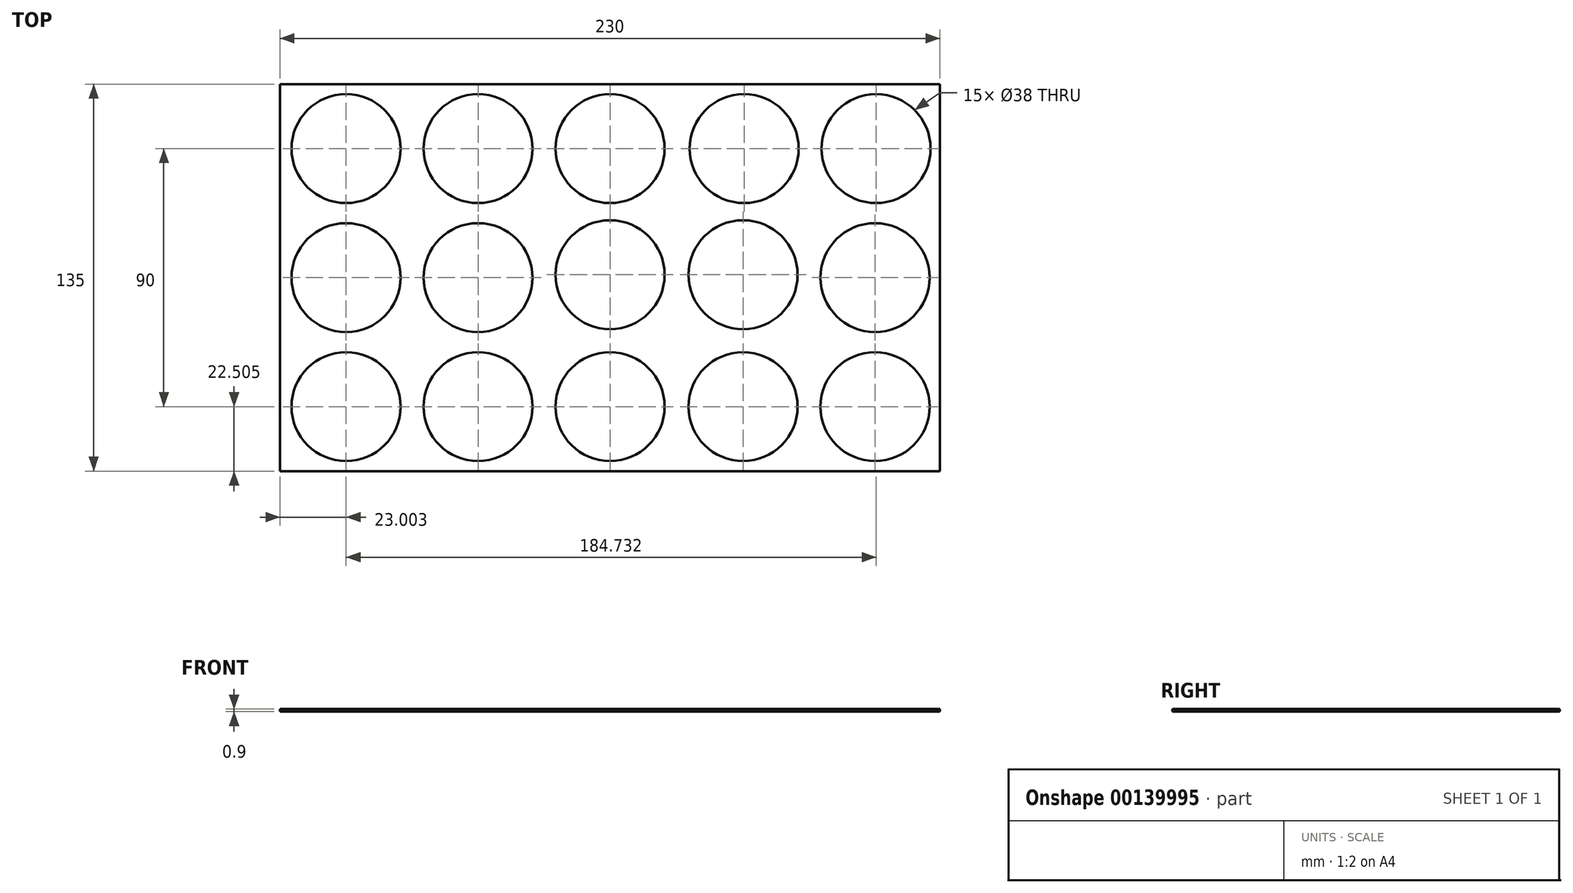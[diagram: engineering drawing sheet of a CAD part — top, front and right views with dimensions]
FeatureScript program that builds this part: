
annotation { "Feature Type Name" : "Feature", "Feature Type Description" : "" }
export const myFeature = defineFeature(function(context is Context, id is Id, definition is map)
    precondition{}
    {
        {
            var Q0;
            Q0=qCreatedBy(makeId("Top.planeOp"),FACE);
            var sketch = newSketch(context, id + "F0", { "sketchPlane" : qUnion([Q0])});
            skLineSegment(sketch, "E0.bottom", {"start": v(-102.59, 50.68) * mm, "end": v(127.41, 50.68) * mm});
            skLineSegment(sketch, "E0.top", {"start": v(-102.59, -84.32) * mm, "end": v(127.41, -84.32) * mm});
            skLineSegment(sketch, "E0.left", {"start": v(-102.59, 50.68) * mm, "end": v(-102.59, -84.32) * mm});
            skLineSegment(sketch, "E0.right", {"start": v(127.41, 50.68) * mm, "end": v(127.41, -84.32) * mm});
            skLineSegment(sketch, "E1", {"start": v(-102.59, -84.32) * mm, "end": v(-102.59, -39.32) * mm});
            skLineSegment(sketch, "E2", {"start": v(-102.59, -39.32) * mm, "end": v(-102.59, 5.68) * mm});
            skLineSegment(sketch, "E3", {"start": v(-102.59, 5.68) * mm, "end": v(-102.59, 50.68) * mm});
            skLineSegment(sketch, "E4", {"start": v(-102.59, -84.32) * mm, "end": v(-56.59, -84.32) * mm});
            skLineSegment(sketch, "E5", {"start": v(-56.59, -84.32) * mm, "end": v(-10.59, -84.32) * mm});
            skLineSegment(sketch, "E6", {"start": v(-10.59, -84.32) * mm, "end": v(35.41, -84.32) * mm});
            skLineSegment(sketch, "E7", {"start": v(35.41, -84.32) * mm, "end": v(81.41, -84.32) * mm});
            skLineSegment(sketch, "E8", {"start": v(81.41, -84.32) * mm, "end": v(127.41, -84.32) * mm});
            skCircle(sketch, "E9", {"center": v(-79.59, 28.18) * mm, "radius": 19 * mm});
            skCircle(sketch, "E10", {"center": v(-33.59, 28.18) * mm, "radius": 19 * mm});
            skCircle(sketch, "E11", {"center": v(12.41, 28.18) * mm, "radius": 19 * mm});
            skCircle(sketch, "E12", {"center": v(59.15, 28.18) * mm, "radius": 19 * mm});
            skCircle(sketch, "E13", {"center": v(105.15, 28.18) * mm, "radius": 19 * mm});
            skCircle(sketch, "E14", {"center": v(104.78, -16.82) * mm, "radius": 19 * mm});
            skCircle(sketch, "E15", {"center": v(104.78, -61.82) * mm, "radius": 19 * mm});
            skCircle(sketch, "E16", {"center": v(58.78, -61.82) * mm, "radius": 19 * mm});
            skCircle(sketch, "E17", {"center": v(58.78, -15.8) * mm, "radius": 19 * mm});
            skCircle(sketch, "E18", {"center": v(12.41, -15.8) * mm, "radius": 19 * mm});
            skCircle(sketch, "E19", {"center": v(12.41, -61.82) * mm, "radius": 19 * mm});
            skCircle(sketch, "E20", {"center": v(-33.59, -61.82) * mm, "radius": 19 * mm});
            skCircle(sketch, "E21", {"center": v(-33.59, -16.82) * mm, "radius": 19 * mm});
            skCircle(sketch, "E22", {"center": v(-79.59, -16.82) * mm, "radius": 19 * mm});
            skCircle(sketch, "E23", {"center": v(-79.59, -61.82) * mm, "radius": 19 * mm});
            skPoint(sketch, "E24", {"position": v(-56.59, -39.32) * mm});
            skPoint(sketch, "E25", {"position": v(-10.59, -39.32) * mm});
            skPoint(sketch, "E26", {"position": v(35.41, -39.32) * mm});
            skPoint(sketch, "E27", {"position": v(-14.59, -17.06) * mm});
            skPoint(sketch, "E28", {"position": v(-56.59, 5.68) * mm});
            skPoint(sketch, "E29", {"position": v(35.41, 5.68) * mm});
            skPoint(sketch, "E30", {"position": v(81.41, 5.68) * mm});
            skPoint(sketch, "E31", {"position": v(81.41, -39.32) * mm});
            skCircle(sketch, "E32", {"center": v(-56.59, -39.32) * mm, "radius": 2.5 * mm});
            skCircle(sketch, "E33", {"center": v(-10.59, -39.32) * mm, "radius": 2.5 * mm});
            skCircle(sketch, "E34", {"center": v(35.41, -39.32) * mm, "radius": 2.5 * mm});
            skCircle(sketch, "E35", {"center": v(81.41, -39.32) * mm, "radius": 2.5 * mm});
            skCircle(sketch, "E36", {"center": v(81.41, 5.68) * mm, "radius": 2.5 * mm});
            skCircle(sketch, "E37", {"center": v(35.41, 5.68) * mm, "radius": 2.5 * mm});
            skCircle(sketch, "E38", {"center": v(-56.59, 5.68) * mm, "radius": 2.5 * mm});
            skPoint(sketch, "E39", {"position": v(-10.59, 5.68) * mm});
            skCircle(sketch, "E40", {"center": v(-10.59, 5.68) * mm, "radius": 2.5 * mm});
            skSolve(sketch);
        }
        {
            var Q0;
            Q0=makeQuery(id+"F0.imprint","IMPRINT",FACE,{"disambiguationData":[TD([[makeQuery(id+"F0.imprint","IMPRINT",EDGE,{"derivedFrom":sQuery(id+"F0.wireOp",EDGE,"E0.bottom")}),-1.0]])]});
            extrude(context, id + "F1", {"entities" : qUnion([Q0]), "depth" : 0.9 * mm});
        }
        {
            var Q0;
            Q0=sQuery(id+"F0.wireOp",EDGE,"E38");
            var Q1;
            Q1=sQuery(id+"F0.wireOp",EDGE,"E32");
            var Q2;
            Q2=sQuery(id+"F0.wireOp",EDGE,"E33");
            var Q3;
            Q3=sQuery(id+"F0.wireOp",EDGE,"E40");
            var Q4;
            Q4=sQuery(id+"F0.wireOp",EDGE,"E37");
            var Q5;
            Q5=sQuery(id+"F0.wireOp",EDGE,"E34");
            var Q6;
            Q6=sQuery(id+"F0.wireOp",EDGE,"E35");
            var Q7;
            Q7=sQuery(id+"F0.wireOp",EDGE,"E36");
            extrude(context, id + "F2", {"bodyType" : ToolBodyType.SURFACE, "surfaceEntities" : qUnion([Q0, Q1, Q2, Q3, Q4, Q5, Q6, Q7]), "oppositeDirection" : true, "depth" : 27 * mm});
        }
        {
            var Q0;
            Q0=makeQuery(id+"F0.imprint","IMPRINT",FACE,{"disambiguationData":[TD([[makeQuery(id+"F0.imprint","IMPRINT",EDGE,{"derivedFrom":sQuery(id+"F0.wireOp",EDGE,"E34")}),1.0]])]});
            var Q1;
            Q1=makeQuery(id+"F0.imprint","IMPRINT",FACE,{"disambiguationData":[TD([[makeQuery(id+"F0.imprint","IMPRINT",EDGE,{"derivedFrom":sQuery(id+"F0.wireOp",EDGE,"E35")}),1.0]])]});
            var Q2;
            Q2=makeQuery(id+"F0.imprint","IMPRINT",FACE,{"disambiguationData":[TD([[makeQuery(id+"F0.imprint","IMPRINT",EDGE,{"derivedFrom":sQuery(id+"F0.wireOp",EDGE,"E36")}),1.0]])]});
            var Q3;
            Q3=makeQuery(id+"F0.imprint","IMPRINT",FACE,{"disambiguationData":[TD([[makeQuery(id+"F0.imprint","IMPRINT",EDGE,{"derivedFrom":sQuery(id+"F0.wireOp",EDGE,"E37")}),1.0]])]});
            var Q4;
            Q4=makeQuery(id+"F0.imprint","IMPRINT",FACE,{"disambiguationData":[TD([[makeQuery(id+"F0.imprint","IMPRINT",EDGE,{"derivedFrom":sQuery(id+"F0.wireOp",EDGE,"E40")}),1.0]])]});
            var Q5;
            Q5=makeQuery(id+"F0.imprint","IMPRINT",FACE,{"disambiguationData":[TD([[makeQuery(id+"F0.imprint","IMPRINT",EDGE,{"derivedFrom":sQuery(id+"F0.wireOp",EDGE,"E38")}),1.0]])]});
            var Q6;
            Q6=makeQuery(id+"F0.imprint","IMPRINT",FACE,{"disambiguationData":[TD([[makeQuery(id+"F0.imprint","IMPRINT",EDGE,{"derivedFrom":sQuery(id+"F0.wireOp",EDGE,"E32")}),1.0]])]});
            var Q7;
            Q7=makeQuery(id+"F0.imprint","IMPRINT",FACE,{"disambiguationData":[TD([[makeQuery(id+"F0.imprint","IMPRINT",EDGE,{"derivedFrom":sQuery(id+"F0.wireOp",EDGE,"E33")}),1.0]])]});
            extrude(context, id + "F3", {"entities" : qUnion([Q0, Q1, Q2, Q3, Q4, Q5, Q6, Q7]), "operationType" : NewBodyOperationType.ADD, "depth" : 0.9 * mm});
        }
    });
